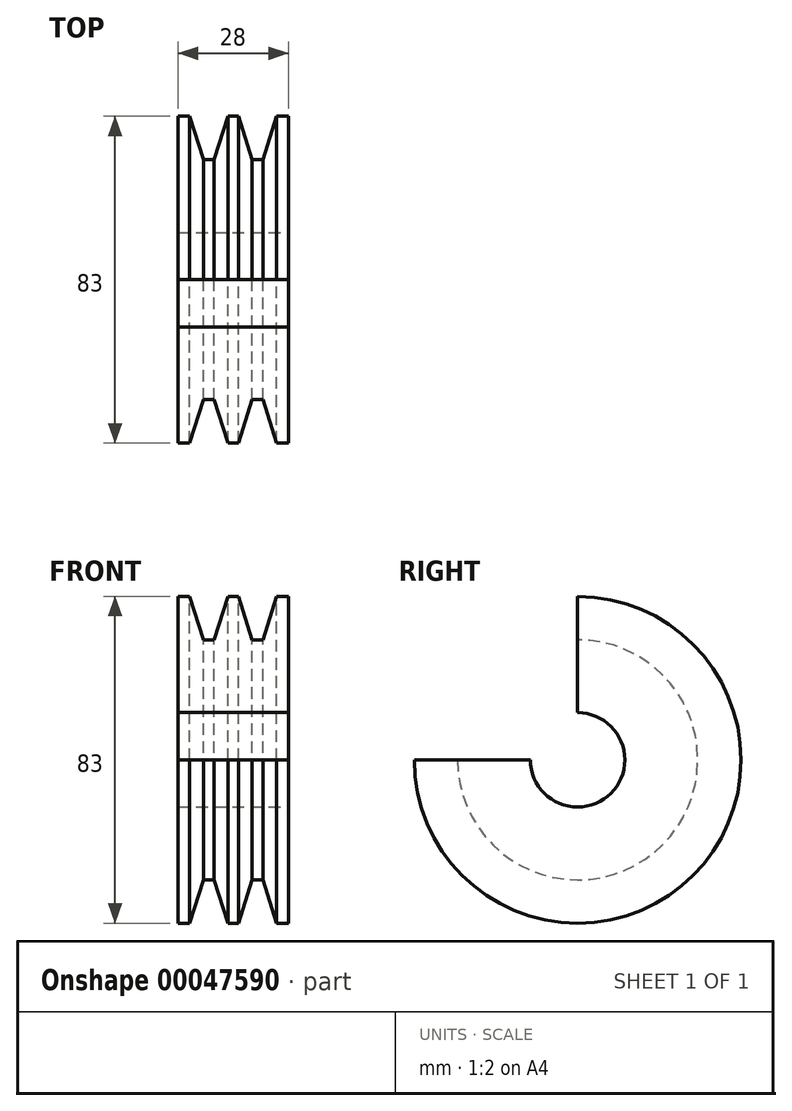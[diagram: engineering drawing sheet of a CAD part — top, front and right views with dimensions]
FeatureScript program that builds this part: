
annotation { "Feature Type Name" : "Feature", "Feature Type Description" : "" }
export const myFeature = defineFeature(function(context is Context, id is Id, definition is map)
    precondition{}
    {
        {
            var Q0;
            Q0=qCreatedBy(makeId("Front.planeOp"),FACE);
            var sketch = newSketch(context, id + "F0", { "sketchPlane" : qUnion([Q0])});
            skLineSegment(sketch, "E0", {"start": v(-44.16, 0) * mm, "end": v(-44.16, 41.5) * mm});
            skLineSegment(sketch, "E1", {"start": v(-44.16, 41.5) * mm, "end": v(-41.2, 41.5) * mm});
            skLineSegment(sketch, "E2", {"start": v(-41.2, 41.5) * mm, "end": v(-37.74, 30.5) * mm});
            skLineSegment(sketch, "E3", {"start": v(-37.74, 30.5) * mm, "end": v(-34.98, 30.5) * mm});
            skLineSegment(sketch, "E4", {"start": v(-34.98, 30.5) * mm, "end": v(-31.5, 41.5) * mm});
            skLineSegment(sketch, "E5", {"start": v(-31.5, 41.5) * mm, "end": v(-28.8, 41.5) * mm});
            skLineSegment(sketch, "E6", {"start": v(-28.8, 41.5) * mm, "end": v(-25.34, 30.5) * mm});
            skLineSegment(sketch, "E7", {"start": v(-25.34, 30.5) * mm, "end": v(-22.58, 30.5) * mm});
            skLineSegment(sketch, "E8", {"start": v(-22.58, 30.5) * mm, "end": v(-19.1, 41.5) * mm});
            skLineSegment(sketch, "E9", {"start": v(-19.1, 41.5) * mm, "end": v(-16.16, 41.5) * mm});
            skLineSegment(sketch, "E10", {"start": v(-16.16, 41.5) * mm, "end": v(-16.16, 0) * mm});
            skLineSegment(sketch, "E11", {"start": v(-16.16, 0) * mm, "end": v(-44.16, 0) * mm});
            skLineSegment(sketch, "E12", {"start": v(-16.16, 12) * mm, "end": v(-44.16, 12) * mm});
            skLineSegment(sketch, "E13", {"start": v(-44.16, 15.3) * mm, "end": v(-16.16, 15.3) * mm});
            skSolve(sketch);
        }
        {
            var Q0;
            {var subQ3=sQuery(id+"F0.wireOp",EDGE,"E1");Q0=makeQuery(id+"F0.imprint","IMPRINT",FACE,{"disambiguationData":[TD([[makeQuery(id+"F0.imprint","IMPRINT",EDGE,{"derivedFrom":subQ3}),-1.0]])]});}
            var Q1;
            {var subQ2=sQuery(id+"F0.wireOp",EDGE,"E12");Q1=makeQuery(id+"F0.imprint","IMPRINT",FACE,{"disambiguationData":[TD([[makeQuery(id+"F0.imprint","IMPRINT",EDGE,{"derivedFrom":subQ2}),-1.0]])]});}
            var Q2;
            Q2=sQuery(id+"F0.wireOp",EDGE,"E11");
            revolve(context, id + "F1", {"entities" : qUnion([Q0, Q1]), "axis" : qUnion([Q2]), "revolveType" : RevolveType.ONE_DIRECTION, "angle" : 270 * degree});
        }
    });
